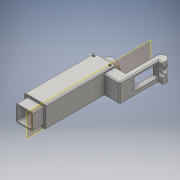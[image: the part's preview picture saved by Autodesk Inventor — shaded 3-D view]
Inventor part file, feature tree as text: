
AUTODESK INVENTOR PART (.ipt)
format: ipt  version: 2016 (Build 200138000, 138)  size: 401,408 bytes
history: native  units: mm
features: extrude x20, sketch x16, fillet x7, other x2, projected_geometry x2
ambient origin geometry x8: Origin, YZ Plane, XZ Plane, XY Plane, X Axis, Y Axis, Z Axis, Center Point
bodies: Body1 (feature_tree)
feature tree (47):
  other  "ソリッド1"
  extrude  "押し出し1"  Depth=31.0mm
  fillet  "フィレット1"  Radius=31.0mm
  extrude  "押し出し2"  Depth=20.0mm TaperAngle=0.0deg
  fillet  "フィレット2"  Radius=2.0mm
  extrude  "押し出し3"  Depth=4.5mm
  extrude  "押し出し5"  Depth=4.5mm
  extrude  "押し出し6"  Depth=4.5mm
  extrude  "押し出し7"  Depth=4.5mm
  extrude  "押し出し8"  Depth=30.0mm TaperAngle=0.0deg
  extrude  "押し出し9"  Depth=2.0mm
  extrude  "押し出し10"  Depth=2.0mm
  extrude  "押し出し11"  Depth=2.5mm
  sketch  "スケッチ11"
  extrude  "押し出し12"  Depth=2.5mm
  extrude  "押し出し13"  Depth=2.5mm
  extrude  "押し出し14"  Depth=2.5mm
  extrude  "押し出し15"  Depth=30.0mm TaperAngle=0.0deg
  extrude  "押し出し25"  Depth=2.0mm
  other  "作業平面1"
  extrude  "押し出し29"  Depth=3.0mm
  extrude  "押し出し30"  Depth=3.0mm
  fillet  "フィレット6"  Radius=3.0mm
  extrude  "押し出し31"  Depth=3.0mm
  extrude  "押し出し33"  Depth=90.0mm TaperAngle=0.0deg
  extrude  "押し出し34"  Depth=10.0mm TaperAngle=0.0deg
  fillet  "フィレット8"  Radius=30.0mm
  fillet  "フィレット9"  Radius=15.0mm
  fillet  "フィレット10"  Radius=3.0mm
  fillet  "フィレット11"  Radius=30.0mm
  sketch  "スケッチ1"
  sketch  "スケッチ2"
  sketch  "スケッチ3"
  sketch  "スケッチ5"
  sketch  "スケッチ6"
  sketch  "スケッチ7"
  sketch  "スケッチ8"
  sketch  "スケッチ9"
  sketch  "スケッチ10"
  sketch  "スケッチ21"
  sketch  "スケッチ24"
  sketch  "スケッチ25"
  sketch  "スケッチ26"
  projected_geometry  "投影ループ1"
  sketch  "スケッチ28"
  sketch  "スケッチ29"
  projected_geometry  "投影ループ3"
